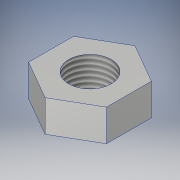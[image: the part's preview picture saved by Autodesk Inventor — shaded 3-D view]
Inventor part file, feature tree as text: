
AUTODESK INVENTOR PART (.ipt)
format: ipt  version: 2018 (Build 220112000, 112)  size: 103,936 bytes
history: native  units: in
note: dims shown in document units (in); Inventor stores cm internally (conversion verified against a paired STEP export)
features: extrude x1, thread x1, sketch x1
ambient origin geometry x8: Origin, YZ Plane, XZ Plane, XY Plane, X Axis, Y Axis, Z Axis, Center Point
bodies: Solid1 (feature_tree)
feature tree (3):
  extrude  "Extrusion1"  Depth=0.112in
  thread  "Thread1"  [1 undecoded]
  sketch  "Sketch1"  dims[d0=0.275in d1=0.15in d2=0.112in d3=0.0in d4=1.0in d5=0.0in]
note: 1 required parameter value undecoded (feature->parameter linkage not recoverable at this tier; creation-order binding heuristic only, values carry confidence <= 0.55)
